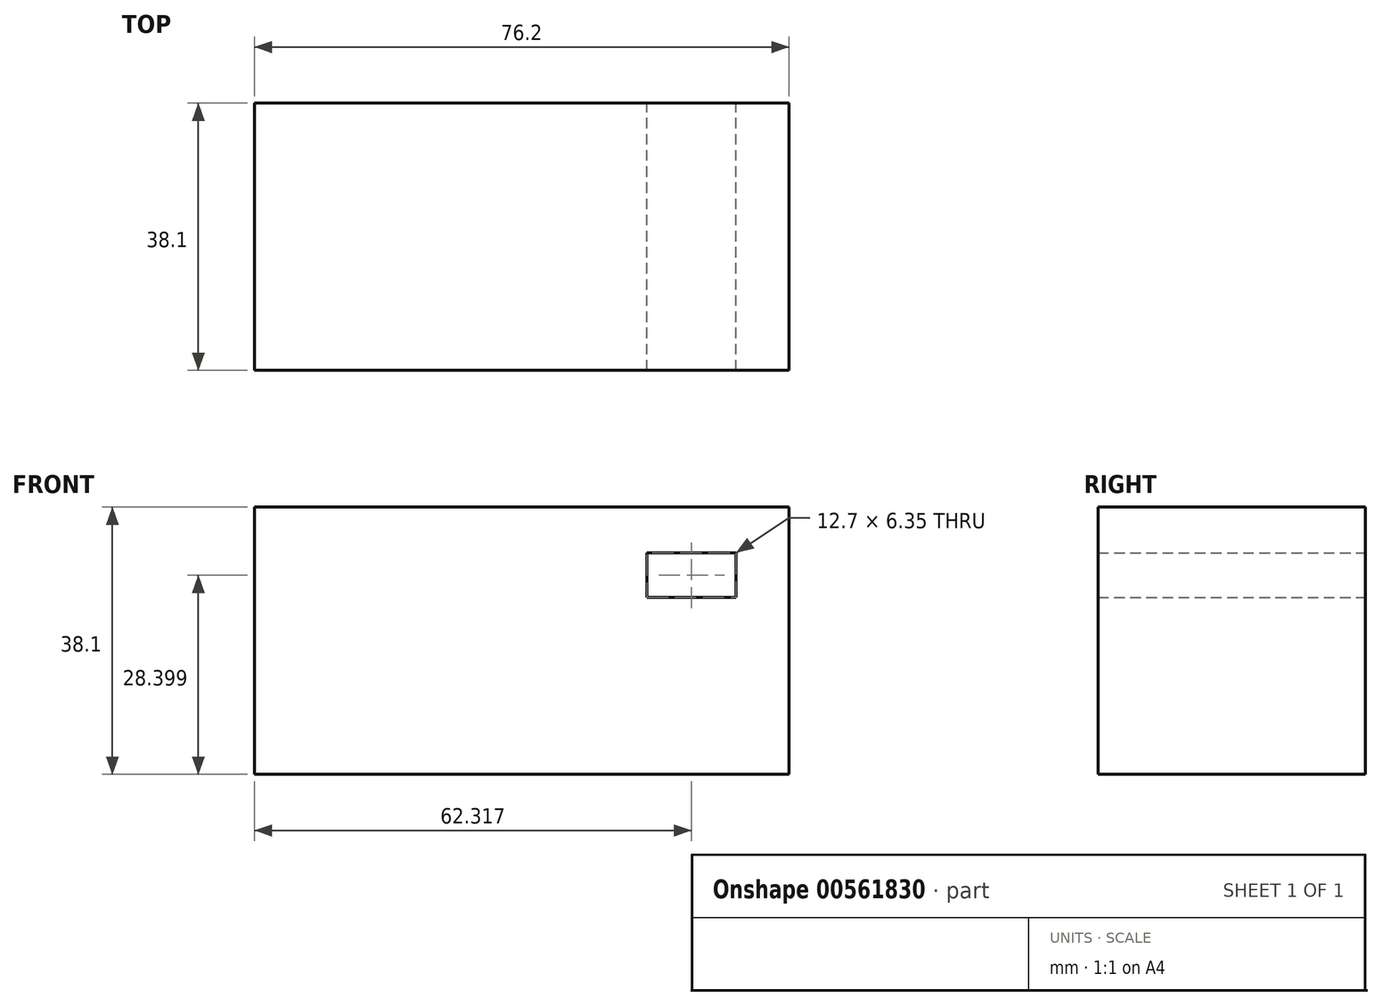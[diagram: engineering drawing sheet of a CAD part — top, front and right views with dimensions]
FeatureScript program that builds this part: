
annotation { "Feature Type Name" : "Feature", "Feature Type Description" : "" }
export const myFeature = defineFeature(function(context is Context, id is Id, definition is map)
    precondition{}
    {
        {
            var Q0;
            Q0=qCreatedBy(makeId("Front.planeOp"),FACE);
            var sketch = newSketch(context, id + "F0", { "sketchPlane" : qUnion([Q0])});
            skLineSegment(sketch, "E0.bottom", {"start": v(-62.47, 42.83) * mm, "end": v(13.73, 42.83) * mm});
            skLineSegment(sketch, "E0.top", {"start": v(-62.47, 4.73) * mm, "end": v(13.73, 4.73) * mm});
            skLineSegment(sketch, "E0.left", {"start": v(-62.47, 42.83) * mm, "end": v(-62.47, 4.73) * mm});
            skLineSegment(sketch, "E0.right", {"start": v(13.73, 42.83) * mm, "end": v(13.73, 4.73) * mm});
            skLineSegment(sketch, "E1.bottom", {"start": v(-6.5, 36.3) * mm, "end": v(6.2, 36.3) * mm});
            skLineSegment(sketch, "E1.top", {"start": v(-6.5, 29.95) * mm, "end": v(6.2, 29.95) * mm});
            skLineSegment(sketch, "E1.left", {"start": v(-6.5, 36.3) * mm, "end": v(-6.5, 29.95) * mm});
            skLineSegment(sketch, "E1.right", {"start": v(6.2, 36.3) * mm, "end": v(6.2, 29.95) * mm});
            skSolve(sketch);
        }
        {
            var Q0;
            Q0=makeQuery(id+"F0.imprint","IMPRINT",FACE,{"disambiguationData":[TD([[makeQuery(id+"F0.imprint","IMPRINT",EDGE,{"derivedFrom":sQuery(id+"F0.wireOp",EDGE,"E0.bottom")}),-1.0]])]});
            extrude(context, id + "F1", {"entities" : qUnion([Q0]), "depth" : 38.1 * mm, "offsetDistance" : 25.4 * mm});
        }
        {
            var Q0;
            Q0=makeQuery(id+"F1.opExtrude","CAP_FACE",FACE,{"disambiguationData":[OSD([sQuery(id+"F0.wireOp",EDGE,"E0.bottom"),sQuery(id+"F0.wireOp",EDGE,"E0.top"),sQuery(id+"F0.wireOp",EDGE,"E0.left"),sQuery(id+"F0.wireOp",EDGE,"E0.right"),sQuery(id+"F0.wireOp",EDGE,"E1.bottom"),sQuery(id+"F0.wireOp",EDGE,"E1.top"),sQuery(id+"F0.wireOp",EDGE,"E1.left"),sQuery(id+"F0.wireOp",EDGE,"E1.right")])],"isStart":false});
            var sketch = newSketch(context, id + "F2", { "sketchPlane" : qUnion([Q0])});
            skCircle(sketch, "E2", {"center": v(-37.25, 22.66) * mm, "radius": 13.93 * mm});
            skSolve(sketch);
        }
        {
            var Q0;
            Q0 = qSketchRegion(id + "F2", true);
            var Q1;
            Q1=sQuery(id+"F2.wireOp",EDGE,"E2");
            extrude(context, id + "F3", {"entities" : qUnion([Q0]), "bodyType" : ToolBodyType.SURFACE, "operationType" : NewBodyOperationType.ADD, "surfaceEntities" : qUnion([Q1]), "depth" : 12.7 * mm, "offsetDistance" : 25.4 * mm});
        }
    });
